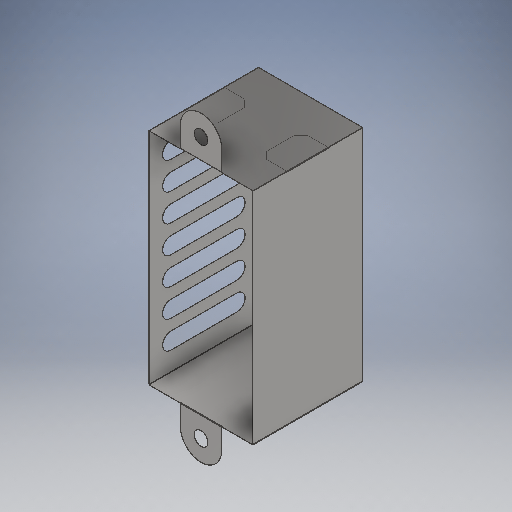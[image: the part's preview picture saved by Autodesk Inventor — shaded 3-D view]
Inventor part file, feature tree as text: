
AUTODESK INVENTOR PART (.ipt)
format: ipt  version: 2025.2 (Build 292293000, 293)  size: 646,144 bytes
history: native  units: mm
features: sheet_metal_op x15, other x9, sketch x9, mirror x2, chamfer x1
ambient origin geometry x8: Origin, YZ Plane, XZ Plane, XY Plane, X Axis, Y Axis, Z Axis, Center Point
bodies: Body1 (feature_tree)
feature tree (36):
  sheet_metal_op  "Face1"
  other  "Grill2"
  sheet_metal_op  "Flange1"
  sheet_metal_op  "Flange2"
  chamfer  "Corner Round1"
  mirror  "Mirror1"
  sheet_metal_op  "Flange3"
  sheet_metal_op  "Flange4"
  other  "Corner Chamfer1"
  mirror  "Mirror2"
  sheet_metal_op  "Unfold5"
  sheet_metal_op  "Refold1"
  sketch  "Sketch3"  dims[d31=0.5mm]
  other  "Plate1"
  sketch  "Sketch4"  dims[d35=63.5mm]
  sketch  "Sketch5"  dims[d36=25.4mm]
  other  "Plate2"
  sheet_metal_op  "Bend1"
  sheet_metal_op  "Corner1"
  sketch  "Sketch6"  dims[d37=6.35mm]
  other  "Plate3"
  sheet_metal_op  "Bend2"
  sheet_metal_op  "Corner2"
  sketch  "Sketch7"  dims[d38=0.5mm]
  sketch  "Sketch8"  dims[d39=0.0mm d40=0.0mm d41=0.5mm]
  other  "Plate4"
  sheet_metal_op  "Bend3"
  sheet_metal_op  "Corner3"
  sketch  "Sketch9"  dims[d42=0.0mm d43=6.35mm d44=0.0mm d45=0.0mm d46=1.0mm d47=0.0mm d48=0.0mm d49=0.0mm d50=863.12561mm]
  other  "Plate5"
  sheet_metal_op  "Bend4"
  sheet_metal_op  "Corner4"
  sketch  "Sketch11"  dims[d51=0.5mm d52=0.25mm d53=1.0mm d54=0.5mm d55=203.2mm d56=90.0deg d57=0.5mm d58=2.0mm d59=0.5mm d60=0.5mm d61=0.5mm d62=0.25mm d63=1.0mm d64=0.5mm d65=76.2mm d66=90.0deg d67=0.5mm d68=76.2mm d69=2.0mm d70=0.5mm d71=0.5mm d72=38.1mm d73=25.4mm d74=0.5mm d75=0.0mm d76=0.5mm d77=0.25mm d78=1.0mm d79=0.5mm d80=203.2mm d81=90.0deg d82=0.5mm d83=2.0mm d84=0.5mm d85=0.5mm d86=0.5mm d87=0.25mm d88=1.0mm d89=0.5mm d90=50.8mm d91=90.0deg d92=0.5mm d93=76.2mm d94=2.0mm d95=0.5mm d96=0.5mm d97=12.7mm d98=6.0mm d99=45.0deg d111=30.48mm d112=152.4mm d113=34.5567mm d114=101.1047mm d116=70.0mm d118=50.8mm d119=10.0mm d121=25.4mm d123=34.5633mm d124=0.5mm d125=0.0mm]
  sketch  "Sketch Rectangular Pattern1"  dims[d30=406.4mm]
  other  "Cut1"
  other  "Cut2"
